# Revit family: KNS_KK_Соединитель парапетный_IEK
name_source: partatom
category: Соединительные детали воздуховодов
units: mm (PartAtom-declared; Revit-internal decimal feet)

## family parameters
Всегда вертикально = Да
Заголовок OmniClass = Air Ductwork
На основе рабочей плоскости = Нет
Номер OmniClass = 23.75.70.14
Общий = Нет
При загрузке вырезать с полостями = Нет
Размер круглого соединителя = Использовать диаметр
Тип детали = Соединение

## types (3) — shared parameters
ADSK_URL документации изделия = https://www.iek.ru
ADSK_URL страницы изделия = https://www.iek.ru
ADSK_Версия Revit = 2019
ADSK_Версия семейства = 1.1
ADSK_Группирование = Кабельные короба
ADSK_Единица измерения = шт
ADSK_Завод-изготовитель = IEK
ADSK_Марка = ПРАЙМЕР
ADSK_Материал наименование = ПВХ (PVC)
ADSK_Материал обозначение = Пластик
ADSK_Обозначение = ТУ 27.33.14-004-83135016-2017
IEK_Гарантийный срок = 2 года
IEK_Монтажная температура = -15...+60 °C
IEK_Срок службы = 25 лет
KSI_CMa_Строительные материалы = 01.07.14
KSI_CPr_Строительные изделия = 20.2.05.01
URL = https://www.iek.ru
Изготовитель = IEK

## per-type parameters (varying)
| type | IEK_Описание | Выбор |
| Боковой стык | Соединитель на стык боковой служит для закрытия распила с боков при соединении кабель-каналов на прямой плоскости. | 1 мм |
| Лицевой стык | Соединитель на стык лицевой служит для закрытия распила крышек при соединении кабель-каналов на прямой плоскости. | 2 мм |
| Стандарт | Соединитель на стык КМС служит для соединения двух кабель-каналов одинакового типоразмера на прямой плоскости. | 1 мм |
